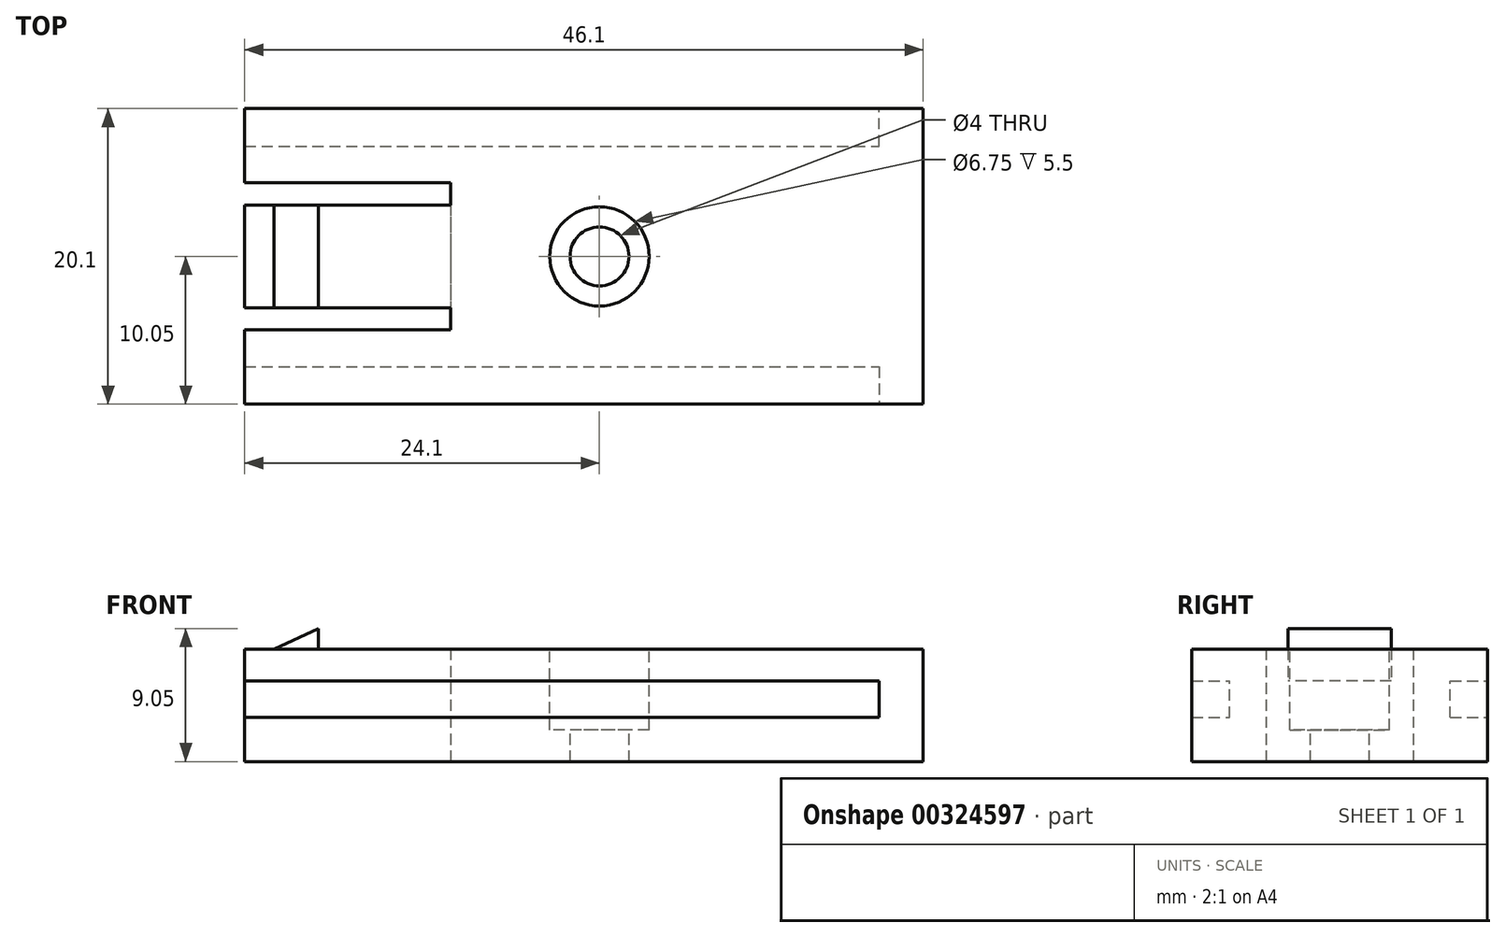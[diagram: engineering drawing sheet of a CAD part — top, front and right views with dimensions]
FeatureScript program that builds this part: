
annotation { "Feature Type Name" : "Feature", "Feature Type Description" : "" }
export const myFeature = defineFeature(function(context is Context, id is Id, definition is map)
    precondition{}
    {
        {
            assignVariable(context, id + "F0", {"name" : "T", "anyValue" : 2.15});
        }
        {
            var Q0;
            Q0=qCreatedBy(makeId("Top.planeOp"),FACE);
            var sketch = newSketch(context, id + "F1", { "sketchPlane" : qUnion([Q0])});
            skLineSegment(sketch, "E0.bottom", {"start": v(-23.05, -10.05) * mm, "end": v(23.05, -10.05) * mm});
            skLineSegment(sketch, "E0.top", {"start": v(-23.05, 10.05) * mm, "end": v(23.05, 10.05) * mm});
            skLineSegment(sketch, "E0.left", {"start": v(-23.05, -10.05) * mm, "end": v(-23.05, 10.05) * mm});
            skLineSegment(sketch, "E0.right", {"start": v(23.05, -10.05) * mm, "end": v(23.05, 10.05) * mm});
            skPoint(sketch, "E0.middle", {"position": v(0, 0) * mm});
            skLineSegment(sketch, "E1", {"start": v(-23.05, 3.5) * mm, "end": v(-9.05, 3.5) * mm});
            skLineSegment(sketch, "E2", {"start": v(-9.05, 3.5) * mm, "end": v(-9.05, 5) * mm});
            skLineSegment(sketch, "E3", {"start": v(-9.05, 5) * mm, "end": v(-23.05, 5) * mm});
            skLineSegment(sketch, "E4", {"start": v(-23.05, -3.5) * mm, "end": v(-9.05, -3.5) * mm});
            skLineSegment(sketch, "E5", {"start": v(-9.05, -3.5) * mm, "end": v(-9.05, -5) * mm});
            skLineSegment(sketch, "E6", {"start": v(-9.05, -5) * mm, "end": v(-23.05, -5) * mm});
            skLineSegment(sketch, "E7", {"start": v(-9.05, 3.5) * mm, "end": v(-9.05, -3.5) * mm, "construction": true});
            skPoint(sketch, "E8", {"position": v(-9.05, 0) * mm});
            skSolve(sketch);
        }
        {
            var Q0;
            {var subQ5=sQuery(id+"F1.wireOp",EDGE,"E0.bottom");Q0=makeQuery(id+"F1.imprint","IMPRINT",FACE,{"disambiguationData":[TD([[makeQuery(id+"F1.imprint","IMPRINT",EDGE,{"derivedFrom":subQ5}),1.0]])]});}
            extrude(context, id + "F2", {"entities" : qUnion([Q0]), "depth" : getVariable(context, 'T') * mm});
        }
        {
            var Q0;
            Q0=makeQuery(id+"F2.opExtrude","CAP_FACE",FACE,{"disambiguationData":[OSD([sQuery(id+"F1.wireOp",EDGE,"E0.bottom"),sQuery(id+"F1.wireOp",EDGE,"E0.top"),sQuery(id+"F1.wireOp",EDGE,"E0.left"),sQuery(id+"F1.wireOp",EDGE,"E0.right"),sQuery(id+"F1.wireOp",EDGE,"E1"),sQuery(id+"F1.wireOp",EDGE,"E2"),sQuery(id+"F1.wireOp",EDGE,"E3"),sQuery(id+"F1.wireOp",EDGE,"E4"),sQuery(id+"F1.wireOp",EDGE,"E5"),sQuery(id+"F1.wireOp",EDGE,"E6")])],"isStart":false});
            var sketch = newSketch(context, id + "F3", { "sketchPlane" : qUnion([Q0])});
            skLineSegment(sketch, "E9", {"start": v(-18.05, 3.5) * mm, "end": v(-18.05, -3.5) * mm});
            skLineSegment(sketch, "E10", {"start": v(-21.05, 3.5) * mm, "end": v(-21.05, -3.5) * mm});
            skSolve(sketch);
        }
        {
            var Q0;
            {var subQ0=sQuery(id+"F3.wireOp",EDGE,"E9");Q0=makeQuery(id+"F3.imprint","IMPRINT",FACE,{"disambiguationData":[TD([[makeQuery(id+"F3.imprint","IMPRINT",EDGE,{"derivedFrom":subQ0}),-1.0]])]});}
            extrude(context, id + "F4", {"entities" : qUnion([Q0]), "operationType" : NewBodyOperationType.ADD, "depth" : 1.4 * mm});
        }
        {
            var Q0;
            Q0=makeQuery(id+"F4.opExtrude","CAP_EDGE",EDGE,{"disambiguationData":[OSD([sQuery(id+"F3.wireOp",EDGE,"E10")])],"isStart":false});
            chamfer(context, id + "F5", {"entities" : qUnion([Q0]), "chamferType" : ChamferType.TWO_OFFSETS, "width1" : 3 * mm, "oppositeDirection" : false, "width2" : 1.4 * mm, "tangentPropagation" : true});
        }
        {
            var Q0;
            Q0=makeQuery(id+"F2.opExtrude","CAP_FACE",FACE,{"disambiguationData":[OSD([sQuery(id+"F1.wireOp",EDGE,"E0.bottom"),sQuery(id+"F1.wireOp",EDGE,"E0.top"),sQuery(id+"F1.wireOp",EDGE,"E0.left"),sQuery(id+"F1.wireOp",EDGE,"E0.right"),sQuery(id+"F1.wireOp",EDGE,"E1"),sQuery(id+"F1.wireOp",EDGE,"E2"),sQuery(id+"F1.wireOp",EDGE,"E3"),sQuery(id+"F1.wireOp",EDGE,"E4"),sQuery(id+"F1.wireOp",EDGE,"E5"),sQuery(id+"F1.wireOp",EDGE,"E6")])],"isStart":true});
            var sketch = newSketch(context, id + "F6", { "sketchPlane" : qUnion([Q0])});
            skLineSegment(sketch, "E11", {"start": v(-23.05, -7.5) * mm, "end": v(23.05, -7.5) * mm});
            skLineSegment(sketch, "E12", {"start": v(-23.05, 7.5) * mm, "end": v(23.05, 7.5) * mm});
            skLineSegment(sketch, "E13", {"start": v(-7.36, -7.5) * mm, "end": v(-7.36, -10.05) * mm, "construction": true});
            skLineSegment(sketch, "E14", {"start": v(-7.36, 7.5) * mm, "end": v(-7.36, 10.05) * mm, "construction": true});
            skPoint(sketch, "E14.startSnap0", {"position": v(-7.36, -8.78) * mm});
            skLineSegment(sketch, "E15", {"start": v(-9.05, -3.5) * mm, "end": v(-9.05, 3.5) * mm});
            skLineSegment(sketch, "E16", {"start": v(20.05, 7.5) * mm, "end": v(20.05, 10.05) * mm});
            skLineSegment(sketch, "E17", {"start": v(20.05, -7.5) * mm, "end": v(20.05, -10.05) * mm});
            skSolve(sketch);
        }
        {
            var Q0;
            {var subQ0=sQuery(id+"F6.wireOp",EDGE,"E11");Q0=makeQuery(id+"F6.imprint","IMPRINT",FACE,{"disambiguationData":[TD([[makeQuery(id+"F6.imprint","IMPRINT",EDGE,{"derivedFrom":subQ0}),1.0]])]});}
            var Q1;
            {var subQ3=sQuery(id+"F6.wireOp",EDGE,"E16");Q1=makeQuery(id+"F6.imprint","IMPRINT",FACE,{"disambiguationData":[TD([[makeQuery(id+"F6.imprint","IMPRINT",EDGE,{"derivedFrom":subQ3}),-1.0]])]});}
            var Q2;
            {var subQ3=sQuery(id+"F6.wireOp",EDGE,"E17");Q2=makeQuery(id+"F6.imprint","IMPRINT",FACE,{"disambiguationData":[TD([[makeQuery(id+"F6.imprint","IMPRINT",EDGE,{"derivedFrom":subQ3}),1.0]])]});}
            extrude(context, id + "F7", {"entities" : qUnion([Q0, Q1, Q2]), "operationType" : NewBodyOperationType.ADD, "depth" : 2.5 * mm});
        }
        {
            var Q0;
            Q0=makeQuery(id+"F7.opExtrude","CAP_FACE",FACE,{"disambiguationData":[OSD([sQuery(id+"F1.wireOp",EDGE,"E0.left"),sQuery(id+"F1.wireOp",EDGE,"E0.right"),sQuery(id+"F1.wireOp",EDGE,"E2"),sQuery(id+"F1.wireOp",EDGE,"E3"),sQuery(id+"F1.wireOp",EDGE,"E5"),sQuery(id+"F1.wireOp",EDGE,"E6"),sQuery(id+"F6.wireOp",EDGE,"E11"),sQuery(id+"F6.wireOp",EDGE,"E12"),sQuery(id+"F6.wireOp",EDGE,"E15")])],"isStart":false});
            var sketch = newSketch(context, id + "F8", { "sketchPlane" : qUnion([Q0])});
            skPoint(sketch, "E18.0", {"position": v(-23.05, -10.05) * mm});
            skLineSegment(sketch, "E19", {"start": v(23.05, 10.05) * mm, "end": v(-23.05, 10.05) * mm});
            skLineSegment(sketch, "E20", {"start": v(-23.05, 10.05) * mm, "end": v(-23.05, 5) * mm});
            skLineSegment(sketch, "E21", {"start": v(-23.05, 5) * mm, "end": v(-9.05, 5) * mm});
            skLineSegment(sketch, "E22", {"start": v(-9.05, 5) * mm, "end": v(-9.05, -5) * mm});
            skLineSegment(sketch, "E23", {"start": v(-9.05, -5) * mm, "end": v(-23.05, -5) * mm});
            skLineSegment(sketch, "E24", {"start": v(-23.05, -5) * mm, "end": v(-23.05, -10.05) * mm});
            skLineSegment(sketch, "E25", {"start": v(23.05, -10.05) * mm, "end": v(-23.05, -10.05) * mm});
            skLineSegment(sketch, "E26", {"start": v(23.05, -10.05) * mm, "end": v(23.05, 10.05) * mm});
            skSolve(sketch);
        }
        {
            var Q0;
            {var subQ0=makeQuery(id+"F7.opExtrude","CAP_EDGE",EDGE,{"disambiguationData":[OSD([sQuery(id+"F6.wireOp",EDGE,"E11")])],"isStart":false});Q0=makeQuery(id+"F8.imprint","IMPRINT",FACE,{"disambiguationData":[TD([[makeQuery(id+"F8.imprint","IMPRINT",EDGE,{"derivedFrom":subQ0}),1.0]])]});}
            var Q1;
            {var subQ1=makeQuery(id+"F7.opExtrude","CAP_EDGE",EDGE,{"disambiguationData":[OSD([sQuery(id+"F6.wireOp",EDGE,"E11")])],"isStart":false});Q1=makeQuery(id+"F8.imprint","IMPRINT",FACE,{"disambiguationData":[TD([[makeQuery(id+"F8.imprint","IMPRINT",EDGE,{"derivedFrom":subQ1}),-1.0]])]});}
            var Q2;
            {var subQ4=makeQuery(id+"F7.opExtrude","CAP_EDGE",EDGE,{"disambiguationData":[OSD([sQuery(id+"F6.wireOp",EDGE,"E12")])],"isStart":false});Q2=makeQuery(id+"F8.imprint","IMPRINT",FACE,{"disambiguationData":[TD([[makeQuery(id+"F8.imprint","IMPRINT",EDGE,{"derivedFrom":subQ4}),1.0]])]});}
            extrude(context, id + "F9", {"entities" : qUnion([Q0, Q1, Q2]), "operationType" : NewBodyOperationType.ADD, "depth" : 3 * mm});
        }
        {
            var Q0;
            {var subQ0=sQuery(id+"F1.wireOp",EDGE,"E5");var subQ1=sQuery(id+"F1.wireOp",EDGE,"E3");var subQ2=sQuery(id+"F1.wireOp",EDGE,"E2");var subQ3=sQuery(id+"F1.wireOp",EDGE,"E4");var subQ4=sQuery(id+"F1.wireOp",EDGE,"E1");var subQ5=sQuery(id+"F1.wireOp",EDGE,"E0.right");var subQ6=sQuery(id+"F1.wireOp",EDGE,"E0.bottom");var subQ7=sQuery(id+"F1.wireOp",EDGE,"E0.top");var subQ8=sQuery(id+"F1.wireOp",EDGE,"E0.left");var subQ9=sQuery(id+"F1.wireOp",EDGE,"E6");Q0=makeQuery(id+"F4.boolean.opBoolean","SPLIT",FACE,{"disambiguationData":[TD([makeQuery(id+"F2.opExtrude","SWEPT_FACE",FACE,{"disambiguationData":[OSD([subQ6])]})])],"derivedFrom":makeQuery(id+"F2.opExtrude","CAP_FACE",FACE,{"disambiguationData":[OSD([subQ6,subQ7,subQ8,subQ5,subQ4,subQ2,subQ1,subQ3,subQ0,subQ9])],"isStart":false})});}
            var sketch = newSketch(context, id + "F10", { "sketchPlane" : qUnion([Q0])});
            skPoint(sketch, "E27", {"position": v(1.05, 0) * mm});
            skSolve(sketch);
        }
        {
            var Q0;
            Q0=sQuery(id+"F10.wireOp",VERTEX,"E27");
            var Q1;
            Q1=makeQuery(id+"F2.opExtrude","SWEPT_BODY",BODY,{"disambiguationData":[OSD([sQuery(id+"F1.wireOp",EDGE,"E0.bottom"),sQuery(id+"F1.wireOp",EDGE,"E0.top"),sQuery(id+"F1.wireOp",EDGE,"E0.left"),sQuery(id+"F1.wireOp",EDGE,"E0.right"),sQuery(id+"F1.wireOp",EDGE,"E1"),sQuery(id+"F1.wireOp",EDGE,"E2"),sQuery(id+"F1.wireOp",EDGE,"E3"),sQuery(id+"F1.wireOp",EDGE,"E4"),sQuery(id+"F1.wireOp",EDGE,"E5"),sQuery(id+"F1.wireOp",EDGE,"E6")])]});
            hole(context, id + "F11", {"style" : HoleStyle.C_BORE, "endStyle" : HoleEndStyle.THROUGH, "holeDiameter" : 4 * mm, "cBoreDiameter" : 6.75 * mm, "cBoreDepth" : 5.5 * mm, "tappedDepth" : 12 * mm, "tapClearance" : 3, "locations" : qUnion([Q0]), "scope" : qUnion([Q1])});
        }
    });
